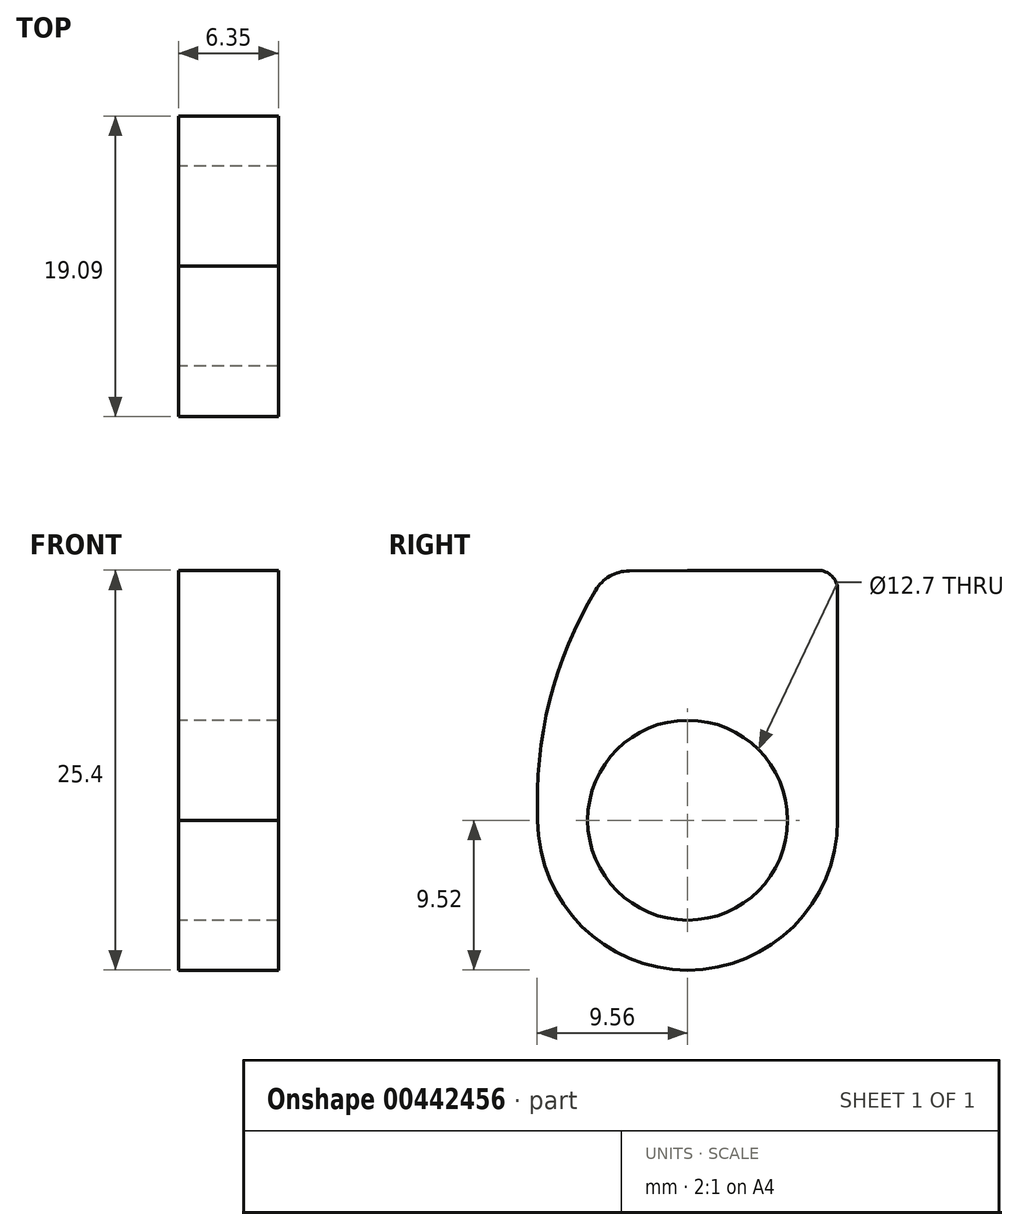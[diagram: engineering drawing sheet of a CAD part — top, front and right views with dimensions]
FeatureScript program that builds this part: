
annotation { "Feature Type Name" : "Feature", "Feature Type Description" : "" }
export const myFeature = defineFeature(function(context is Context, id is Id, definition is map)
    precondition{}
    {
        {
            var Q0;
            Q0=qCreatedBy(makeId("Right.planeOp"),FACE);
            var sketch = newSketch(context, id + "F0", { "sketchPlane" : qUnion([Q0])});
            skCircle(sketch, "E0", {"center": v(0, 0) * mm, "radius": 6.35 * mm});
            skCircle(sketch, "E1", {"center": v(0, 0) * mm, "radius": 9.53 * mm});
            skPoint(sketch, "E2", {"position": v(0, 15.88) * mm});
            skArc(sketch, "E3", {"start": v(-5.86, 14.6) * mm, "mid": v(-8.77, 7.57) * mm, "end": v(-9.52, 0) * mm});
            skLineSegment(sketch, "E4", {"start": v(-3.7, 15.84) * mm, "end": v(0, 15.87) * mm});
            skLineSegment(sketch, "E5", {"start": v(0, 15.87) * mm, "end": v(3.69, 15.88) * mm});
            skPoint(sketch, "E6.visualSharp", {"position": v(-5.08, 15.82) * mm});
            skArc(sketch, "E6.filletArc", {"start": v(-3.7, 15.84) * mm, "mid": v(-4.94, 15.5) * mm, "end": v(-5.86, 14.6) * mm});
            skLineSegment(sketch, "E7", {"start": v(9.53, 0) * mm, "end": v(9.53, 14.6) * mm});
            skLineSegment(sketch, "E8", {"start": v(8.26, 15.88) * mm, "end": v(3.69, 15.88) * mm});
            skPoint(sketch, "E9.visualSharp", {"position": v(9.53, 15.88) * mm});
            skArc(sketch, "E9.filletArc", {"start": v(9.53, 14.6) * mm, "mid": v(9.15, 15.5) * mm, "end": v(8.26, 15.88) * mm});
            skSolve(sketch);
        }
        {
            var Q0;
            Q0 = qSketchRegion(id + "F0", true);
            extrude(context, id + "F1", {"entities" : qUnion([Q0]), "depth" : 6.35 * mm});
        }
    });
